# Revit family: Distribution enclosure Marina cabinet full door
name_source: partatom
category: Equipement électrique
units: mm (PartAtom-declared; Revit-internal decimal feet)

## family parameters
Basée sur le plan de construction = Non
Configuration du panneau = Deux colonnes, circuits au sein
Cote de connecteur circulaire = Utiliser le diamètre
Couper avec des vides une fois chargée = Non
Numéro OmniClass = 23.80.30.11.17
Partagée = Non
Point de calcul de pièce = Non
Titre OmniClass = Distribution Boards and Control Panels
Toujours verticalement = Oui
Type d'élément = Tableau de raccordement

## types (8) — shared parameters
ETIM Class 6.0 = EC000058
Fabricant = Legrand
General Conditions of Use = https://export.legrand.com
IK = 10
IP = 66
Image du type = Coffret_Marina_036263_pw_92782_pz_5.jpg
Material = Polyester
RAL = 7035
URL = www.legrand.fr
zero-valued in all types: Elévation par défaut

## per-type parameters (varying)
| type | Cabinet 036250 | Cabinet 036251 | Cabinet 036252 | Cabinet 036255 | Cabinet 036256 | Cabinet 036261 | Cabinet 036263 | Cabinet 036264 | Description | depth | depth installation zone | distance before installation zone | distance side installation zone | height | weight | width | width installation zone |
| Marina cabinet depth 160 height 300 width 200 | Oui | Non | Non | Non | Non | Non | Non | Non | 036250  Marina cabinet depth 160 height 300 width 200 | 160 mm  [stored 0.524934 ft] | 380 mm  [stored 1.24672 ft] | 220 mm  [stored 0.721785 ft] | 160 mm  [stored 0.524934 ft] | 300 mm | 1.75 kg | 220 mm  [stored 0.721785 ft] | 540 mm  [stored 1.77165 ft] |
| Marina cabinet depth 200 height 400 width 300 | Non | Oui | Non | Non | Non | Non | Non | Non | 036251 Marina cabinet depth 200 height 400 width 300 | 206 mm  [stored 0.675853 ft] | 506 mm  [stored 1.6601 ft] | 300 mm | 206 mm  [stored 0.675853 ft] | 400 mm  [stored 1.31234 ft] | 3.70 kg | 300 mm | 712 mm  [stored 2.33596 ft] |
| Marina cabinet depth 200 height 500 width 400 | Non | Non | Oui | Non | Non | Non | Non | Non | 036252  Marina cabinet depth 200 height 500 width 400 | 206 mm  [stored 0.675853 ft] | 606 mm  [stored 1.98819 ft] | 400 mm  [stored 1.31234 ft] | 206 mm  [stored 0.675853 ft] | 500 mm  [stored 1.64042 ft] | 5.10 kg | 400 mm  [stored 1.31234 ft] | 812 mm  [stored 2.66404 ft] |
| Marina cabinet depth 250 height 600 width 400 | Non | Non | Non | Oui | Non | Non | Non | Non | 036255  Marina cabinet depth 250 height 600 width 400 | 257 mm  [stored 0.843176 ft] | 657 mm | 400 mm  [stored 1.31234 ft] | 257 mm  [stored 0.843176 ft] | 610 mm  [stored 2.00131 ft] | 6.40 kg | 400 mm  [stored 1.31234 ft] | 914 mm |
| Marina cabinet depth 250 height 700 width 500 | Non | Non | Non | Non | Oui | Non | Non | Non | 036256  Marina cabinet depth 250 height 700 width 500 | 250 mm  [stored 0.82021 ft] | 760 mm  [stored 2.49344 ft] | 510 mm  [stored 1.67323 ft] | 250 mm  [stored 0.82021 ft] | 720 mm  [stored 2.3622 ft] | 11.20 kg | 510 mm  [stored 1.67323 ft] | 1010 mm  [stored 3.31365 ft] |
| Marina cabinet depth 300 height 800 width 600 | Non | Non | Non | Non | Non | Oui | Non | Non | 036261  Marina cabinet depth 300 height 800 width 600 | 300 mm | 910 mm | 610 mm  [stored 2.00131 ft] | 300 mm | 820 mm  [stored 2.69029 ft] | 15.20 kg | 610 mm  [stored 2.00131 ft] | 1210 mm |
| Marina cabinet depth 300 height 1000 width 800 | Non | Non | Non | Non | Non | Non | Oui | Non | 036263  Marina cabinet depth 300 height 1000 width 800 | 300 mm | 1110 mm | 810 mm  [stored 2.65748 ft] | 300 mm | 1020 mm  [stored 3.34646 ft] | 21.80 kg | 810 mm  [stored 2.65748 ft] | 1410 mm  [stored 4.62598 ft] |
| Marina cabinet depth 300 height 1200 width 800 | Non | Non | Non | Non | Non | Non | Non | Oui | 036264  Marina cabinet depth 300 height 1200 width 800 | 300 mm | 1110 mm | 810 mm  [stored 2.65748 ft] | 300 mm | 1220 mm  [stored 4.00262 ft] | 25.00 kg | 810 mm  [stored 2.65748 ft] | 1410 mm  [stored 4.62598 ft] |

note: [stored X ft] marks values corroborated as IEEE doubles in the binary element streams (Revit-internal decimal feet)
